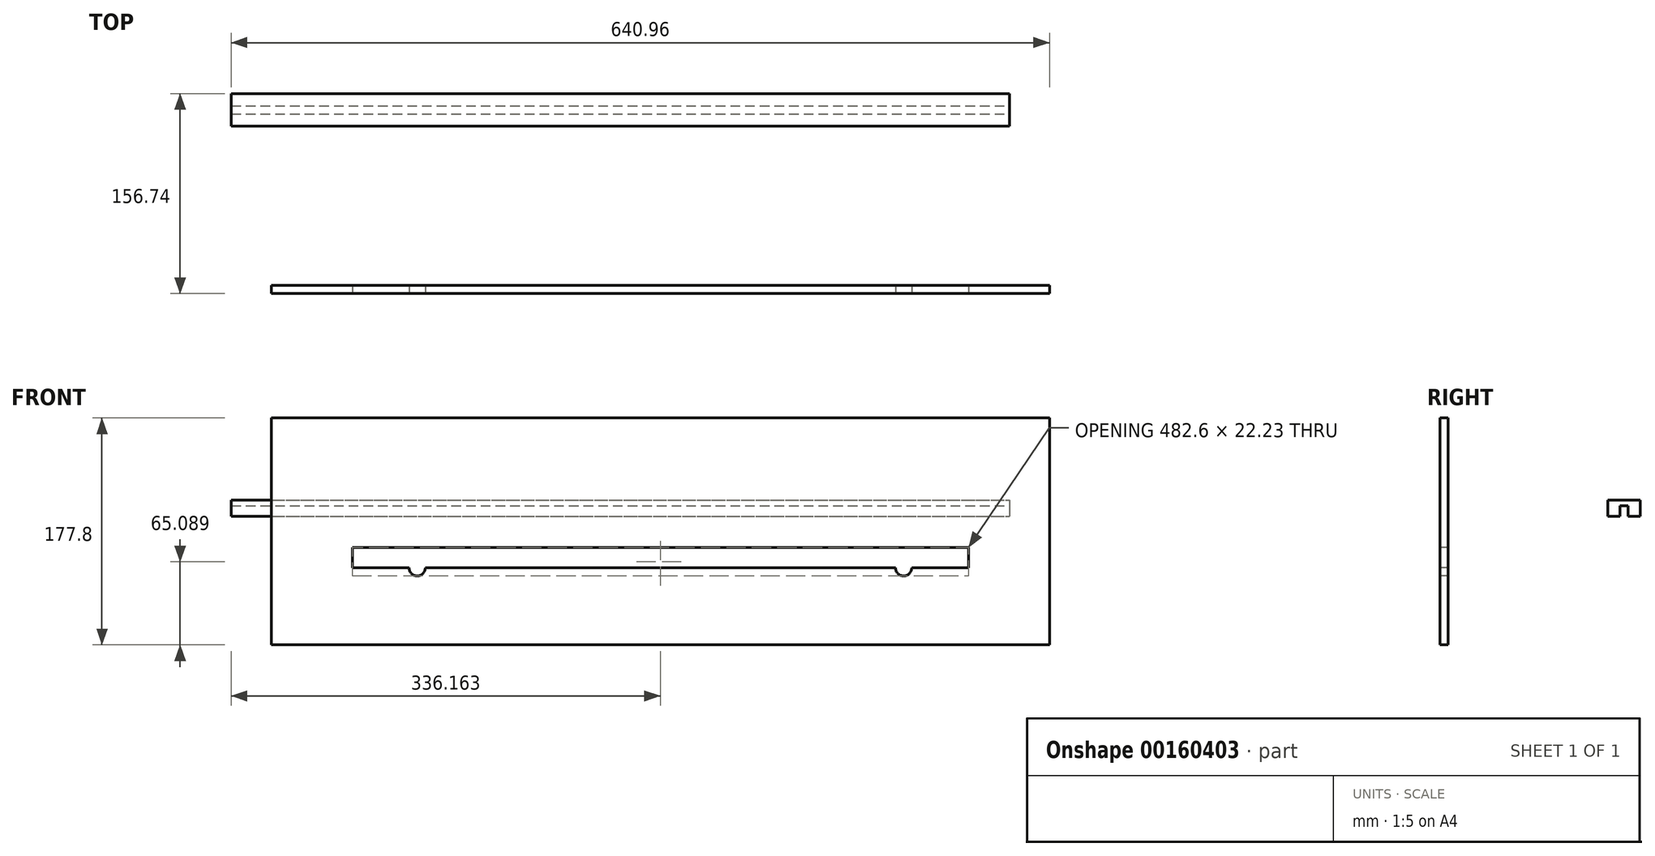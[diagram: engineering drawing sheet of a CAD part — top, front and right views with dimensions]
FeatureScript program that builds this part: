
annotation { "Feature Type Name" : "Feature", "Feature Type Description" : "" }
export const myFeature = defineFeature(function(context is Context, id is Id, definition is map)
    precondition{}
    {
        {
            var Q0;
            Q0=qCreatedBy(makeId("Front.planeOp"),FACE);
            var sketch = newSketch(context, id + "F0", { "sketchPlane" : qUnion([Q0])});
            skLineSegment(sketch, "E0.bottom", {"start": v(-283.76, 76.96) * mm, "end": v(325.84, 76.96) * mm});
            skLineSegment(sketch, "E0.top", {"start": v(-283.76, -100.84) * mm, "end": v(325.84, -100.84) * mm});
            skLineSegment(sketch, "E0.left", {"start": v(-283.76, 76.96) * mm, "end": v(-283.76, -100.84) * mm});
            skLineSegment(sketch, "E0.right", {"start": v(325.84, 76.96) * mm, "end": v(325.84, -100.84) * mm});
            skSolve(sketch);
        }
        {
            var Q0;
            Q0 = qSketchRegion(id + "F0", true);
            extrude(context, id + "F1", {"entities" : qUnion([Q0]), "depth" : 6.35 * mm});
        }
        {
            var Q0;
            Q0=makeQuery(id+"F1.opExtrude","CAP_FACE",FACE,{"disambiguationData":[OSD([sQuery(id+"F0.wireOp",EDGE,"E0.bottom"),sQuery(id+"F0.wireOp",EDGE,"E0.top"),sQuery(id+"F0.wireOp",EDGE,"E0.left"),sQuery(id+"F0.wireOp",EDGE,"E0.right")])],"isStart":false});
            var sketch = newSketch(context, id + "F2", { "sketchPlane" : qUnion([Q0])});
            skLineSegment(sketch, "E1.0", {"start": v(-220.26, 76.96) * mm, "end": v(-220.26, -100.84) * mm, "construction": true});
            skLineSegment(sketch, "E2.0", {"start": v(262.34, 76.96) * mm, "end": v(262.34, -100.84) * mm, "construction": true});
            skLineSegment(sketch, "E3.0", {"start": v(-283.76, -24.64) * mm, "end": v(325.84, -24.64) * mm, "construction": true});
            skLineSegment(sketch, "E4.0", {"start": v(-283.76, -40.51) * mm, "end": v(-175.8, -40.51) * mm, "construction": true});
            skLineSegment(sketch, "E5", {"start": v(-220.26, -24.64) * mm, "end": v(-220.26, -40.51) * mm});
            skLineSegment(sketch, "E6", {"start": v(-220.26, -40.51) * mm, "end": v(-175.8, -40.51) * mm});
            skLineSegment(sketch, "E7", {"start": v(262.34, -40.51) * mm, "end": v(262.34, -24.64) * mm});
            skLineSegment(sketch, "E8", {"start": v(262.34, -24.64) * mm, "end": v(-220.26, -24.64) * mm});
            skLineSegment(sketch, "E9.0", {"start": v(211.54, 76.96) * mm, "end": v(211.54, -100.84) * mm, "construction": true});
            skLineSegment(sketch, "E10.0", {"start": v(-169.46, 76.96) * mm, "end": v(-169.46, -100.84) * mm, "construction": true});
            skArc(sketch, "E11", {"start": v(-175.8, -40.51) * mm, "mid": v(-169.46, -46.86) * mm, "end": v(-163.1, -40.51) * mm});
            skArc(sketch, "E12", {"start": v(205.2, -40.51) * mm, "mid": v(211.54, -46.86) * mm, "end": v(217.9, -40.51) * mm});
            skLineSegment(sketch, "E13.trimOffspring", {"start": v(-163.1, -40.51) * mm, "end": v(205.2, -40.51) * mm});
            skLineSegment(sketch, "E14.trimOffspring", {"start": v(217.9, -40.51) * mm, "end": v(262.34, -40.51) * mm});
            skLineSegment(sketch, "E15.trimOffspring", {"start": v(217.9, -40.51) * mm, "end": v(325.84, -40.51) * mm, "construction": true});
            skLineSegment(sketch, "E16.trimOffspring", {"start": v(-163.1, -40.51) * mm, "end": v(205.2, -40.51) * mm, "construction": true});
            skSolve(sketch);
        }
        {
            var Q0;
            Q0=makeQuery(id+"F2.imprint","IMPRINT",FACE,{"disambiguationData":[TD([[makeQuery(id+"F2.imprint","IMPRINT",EDGE,{"derivedFrom":sQuery(id+"F2.wireOp",EDGE,"E5")}),1.0]])]});
            extrude(context, id + "F3", {"entities" : qUnion([Q0]), "operationType" : NewBodyOperationType.REMOVE, "oppositeDirection" : true, "depth" : 6.35 * mm});
        }
        {
            var Q0;
            Q0=qCreatedBy(makeId("Top.planeOp"),FACE);
            var sketch = newSketch(context, id + "F4", { "sketchPlane" : qUnion([Q0])});
            skLineSegment(sketch, "E17.bottom", {"start": v(-315.12, 150.4) * mm, "end": v(294.48, 150.4) * mm});
            skLineSegment(sketch, "E17.top", {"start": v(-315.12, 125) * mm, "end": v(294.48, 125) * mm});
            skLineSegment(sketch, "E17.left", {"start": v(-315.12, 150.4) * mm, "end": v(-315.12, 125) * mm});
            skLineSegment(sketch, "E17.right", {"start": v(294.48, 150.4) * mm, "end": v(294.48, 125) * mm});
            skSolve(sketch);
        }
        {
            var Q0;
            Q0 = qSketchRegion(id + "F4", true);
            extrude(context, id + "F5", {"entities" : qUnion([Q0]), "depth" : 12.7 * mm});
        }
        {
            var Q0;
            Q0=makeQuery(id+"F5.opExtrude","CAP_FACE",FACE,{"disambiguationData":[OSD([sQuery(id+"F4.wireOp",EDGE,"E17.bottom"),sQuery(id+"F4.wireOp",EDGE,"E17.top"),sQuery(id+"F4.wireOp",EDGE,"E17.left"),sQuery(id+"F4.wireOp",EDGE,"E17.right")])],"isStart":true});
            var sketch = newSketch(context, id + "F6", { "sketchPlane" : qUnion([Q0])});
            skLineSegment(sketch, "E18.0", {"start": v(-315.12, -134.52) * mm, "end": v(294.48, -134.52) * mm, "construction": true});
            skLineSegment(sketch, "E19.0", {"start": v(-315.12, -140.87) * mm, "end": v(294.48, -140.87) * mm, "construction": true});
            skLineSegment(sketch, "E20", {"start": v(-315.12, -134.52) * mm, "end": v(294.48, -134.52) * mm});
            skLineSegment(sketch, "E21", {"start": v(-315.12, -140.87) * mm, "end": v(294.48, -140.87) * mm});
            skSolve(sketch);
        }
        {
            var Q0;
            {var subQ0=sQuery(id+"F6.wireOp",EDGE,"E20");Q0=makeQuery(id+"F6.imprint","IMPRINT",FACE,{"disambiguationData":[TD([[makeQuery(id+"F6.imprint","IMPRINT",EDGE,{"derivedFrom":subQ0}),-1.0]])]});}
            extrude(context, id + "F7", {"entities" : qUnion([Q0]), "operationType" : NewBodyOperationType.REMOVE, "oppositeDirection" : true, "depth" : 8 * mm});
        }
    });
